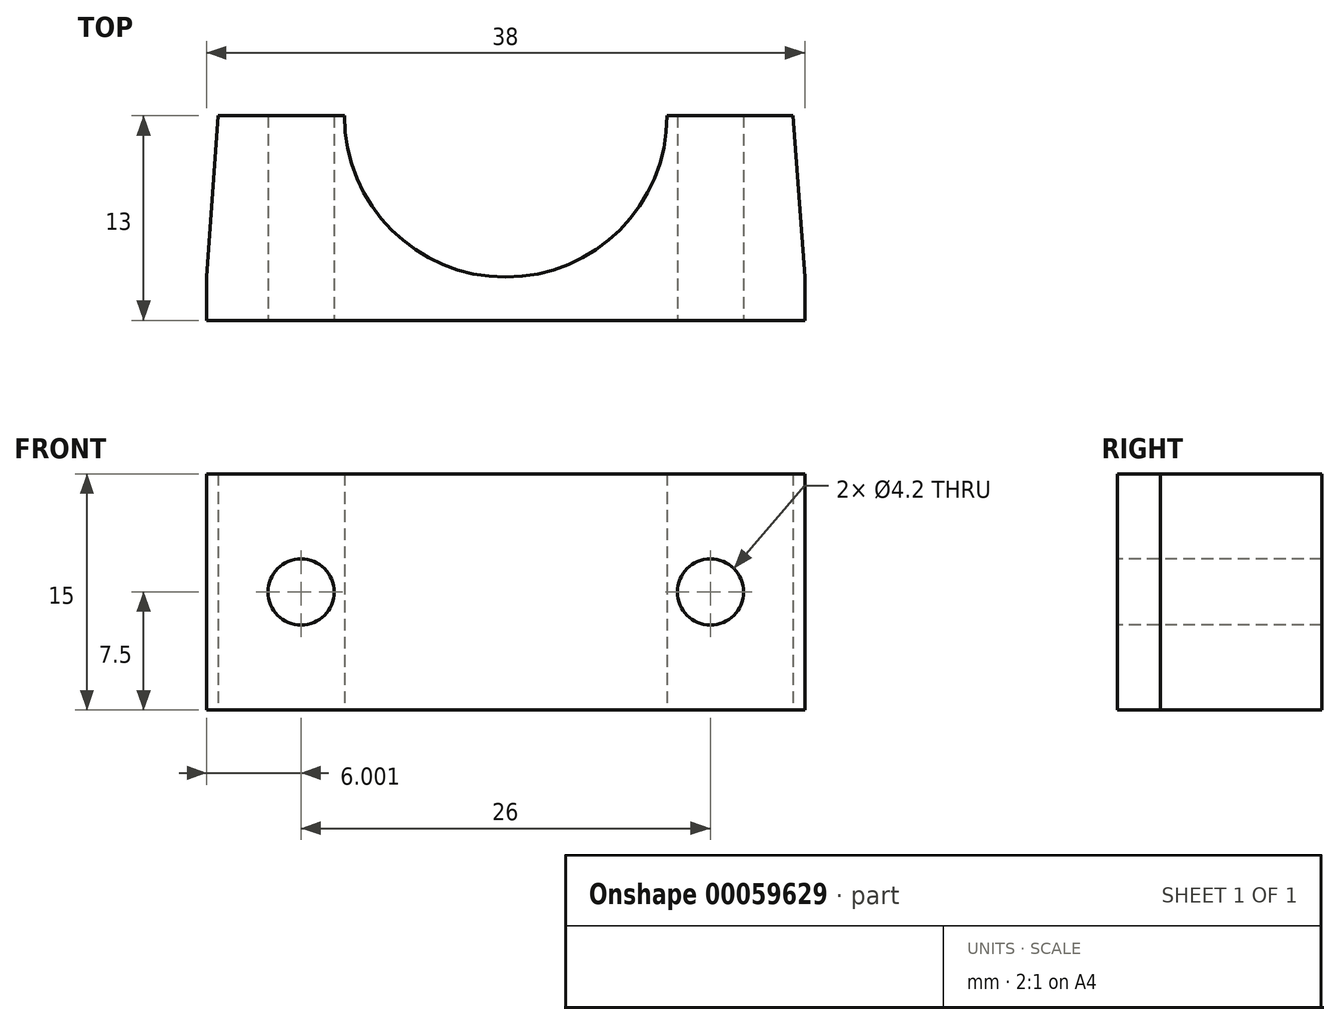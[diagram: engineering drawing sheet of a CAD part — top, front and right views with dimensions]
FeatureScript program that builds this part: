
annotation { "Feature Type Name" : "Feature", "Feature Type Description" : "" }
export const myFeature = defineFeature(function(context is Context, id is Id, definition is map)
    precondition{}
    {
        {
            var Q0;
            Q0=qCreatedBy(makeId("Top.planeOp"),FACE);
            var sketch = newSketch(context, id + "F0", { "sketchPlane" : qUnion([Q0])});
            skLineSegment(sketch, "E0.bottom", {"start": v(-71.36, 11.65) * mm, "end": v(-33.36, 11.65) * mm, "construction": true});
            skLineSegment(sketch, "E0.top", {"start": v(-71.36, 8.9) * mm, "end": v(-33.36, 8.9) * mm});
            skLineSegment(sketch, "E0.left", {"start": v(-71.36, 11.65) * mm, "end": v(-71.36, 8.9) * mm});
            skLineSegment(sketch, "E0.right", {"start": v(-33.36, 11.65) * mm, "end": v(-33.36, 8.9) * mm});
            skArc(sketch, "E1", {"start": v(-42.1, 11.65) * mm, "mid": v(-52.36, 21.9) * mm, "end": v(-62.6, 11.65) * mm, "construction": true});
            skLineSegment(sketch, "E2", {"start": v(-62.6, 21.9) * mm, "end": v(-42.1, 21.9) * mm, "construction": true});
            skArc(sketch, "E3", {"start": v(-42.1, 21.9) * mm, "mid": v(-52.36, 32.15) * mm, "end": v(-62.6, 21.9) * mm, "construction": true});
            skArc(sketch, "E4", {"start": v(-62.6, 21.9) * mm, "mid": v(-52.36, 11.65) * mm, "end": v(-42.1, 21.9) * mm});
            skLineSegment(sketch, "E5.bottom", {"start": v(-62.6, 21.9) * mm, "end": v(-70.6, 21.9) * mm});
            skLineSegment(sketch, "E5.top", {"start": v(-62.6, 17.04) * mm, "end": v(-67.6, 17.04) * mm, "construction": true});
            skLineSegment(sketch, "E5.left", {"start": v(-62.6, 21.9) * mm, "end": v(-62.6, 17.04) * mm, "construction": true});
            skLineSegment(sketch, "E6.bottom", {"start": v(-42.1, 21.9) * mm, "end": v(-34.1, 21.9) * mm});
            skLineSegment(sketch, "E6.top", {"start": v(-42.1, 17.04) * mm, "end": v(-37.1, 17.04) * mm, "construction": true});
            skLineSegment(sketch, "E6.left", {"start": v(-42.1, 21.9) * mm, "end": v(-42.1, 17.04) * mm, "construction": true});
            skLineSegment(sketch, "E7.bottom", {"start": v(-71.36, 11.65) * mm, "end": v(-69.1, 11.65) * mm});
            skLineSegment(sketch, "E8.bottom", {"start": v(-33.36, 11.65) * mm, "end": v(-35.6, 11.65) * mm});
            skLineSegment(sketch, "E9", {"start": v(-70.6, 21.9) * mm, "end": v(-71.36, 11.65) * mm});
            skLineSegment(sketch, "E10", {"start": v(-34.1, 21.9) * mm, "end": v(-33.36, 11.65) * mm});
            skSolve(sketch);
        }
        {
            var Q0;
            Q0=makeQuery(id+"F0.imprint","IMPRINT",FACE,{"disambiguationData":[TD([[makeQuery(id+"F0.imprint","IMPRINT",EDGE,{"derivedFrom":sQuery(id+"F0.wireOp",EDGE,"E0.top")}),1.0]])]});
            extrude(context, id + "F1", {"entities" : qUnion([Q0]), "depth" : 15 * mm});
        }
        {
            var Q0;
            Q0=makeQuery(id+"F1.opExtrude","SWEPT_FACE",FACE,{"disambiguationData":[OSD([sQuery(id+"F0.wireOp",EDGE,"E0.top")])]});
            var sketch = newSketch(context, id + "F2", { "sketchPlane" : qUnion([Q0])});
            skLineSegment(sketch, "E11.bottom", {"start": v(-71.36, 15) * mm, "end": v(-33.36, 15) * mm, "construction": true});
            skLineSegment(sketch, "E11.top", {"start": v(-71.36, 0) * mm, "end": v(-33.36, 0) * mm, "construction": true});
            skLineSegment(sketch, "E11.left", {"start": v(-71.36, 15) * mm, "end": v(-71.36, 0) * mm, "construction": true});
            skLineSegment(sketch, "E11.right", {"start": v(-33.36, 15) * mm, "end": v(-33.36, 0) * mm, "construction": true});
            skLineSegment(sketch, "E12", {"start": v(-71.36, 7.5) * mm, "end": v(-33.36, 7.5) * mm, "construction": true});
            skLineSegment(sketch, "E13", {"start": v(-52.36, 15) * mm, "end": v(-52.36, 0) * mm, "construction": true});
            skPoint(sketch, "E14", {"position": v(-65.36, 7.5) * mm});
            skPoint(sketch, "E15", {"position": v(-39.36, 7.5) * mm});
            skSolve(sketch);
        }
        {
            var Q0;
            Q0=sQuery(id+"F2.wireOp",VERTEX,"E14");
            var Q1;
            Q1=sQuery(id+"F2.wireOp",VERTEX,"E15");
            var Q2;
            Q2=makeQuery(id+"F1.opExtrude","SWEPT_BODY",BODY,{"disambiguationData":[OSD([sQuery(id+"F0.wireOp",EDGE,"E0.top"),sQuery(id+"F0.wireOp",EDGE,"E0.left"),sQuery(id+"F0.wireOp",EDGE,"E0.right"),sQuery(id+"F0.wireOp",EDGE,"E4"),sQuery(id+"F0.wireOp",EDGE,"E5.bottom"),sQuery(id+"F0.wireOp",EDGE,"E6.bottom"),sQuery(id+"F0.wireOp",EDGE,"E9"),sQuery(id+"F0.wireOp",EDGE,"E10")])]});
            hole(context, id + "F3", {"style" : HoleStyle.SIMPLE, "holeDiameter" : 4.2 * mm, "endStyle" : HoleEndStyle.THROUGH, "locations" : qUnion([Q0, Q1]), "scope" : qUnion([Q2])});
        }
    });
